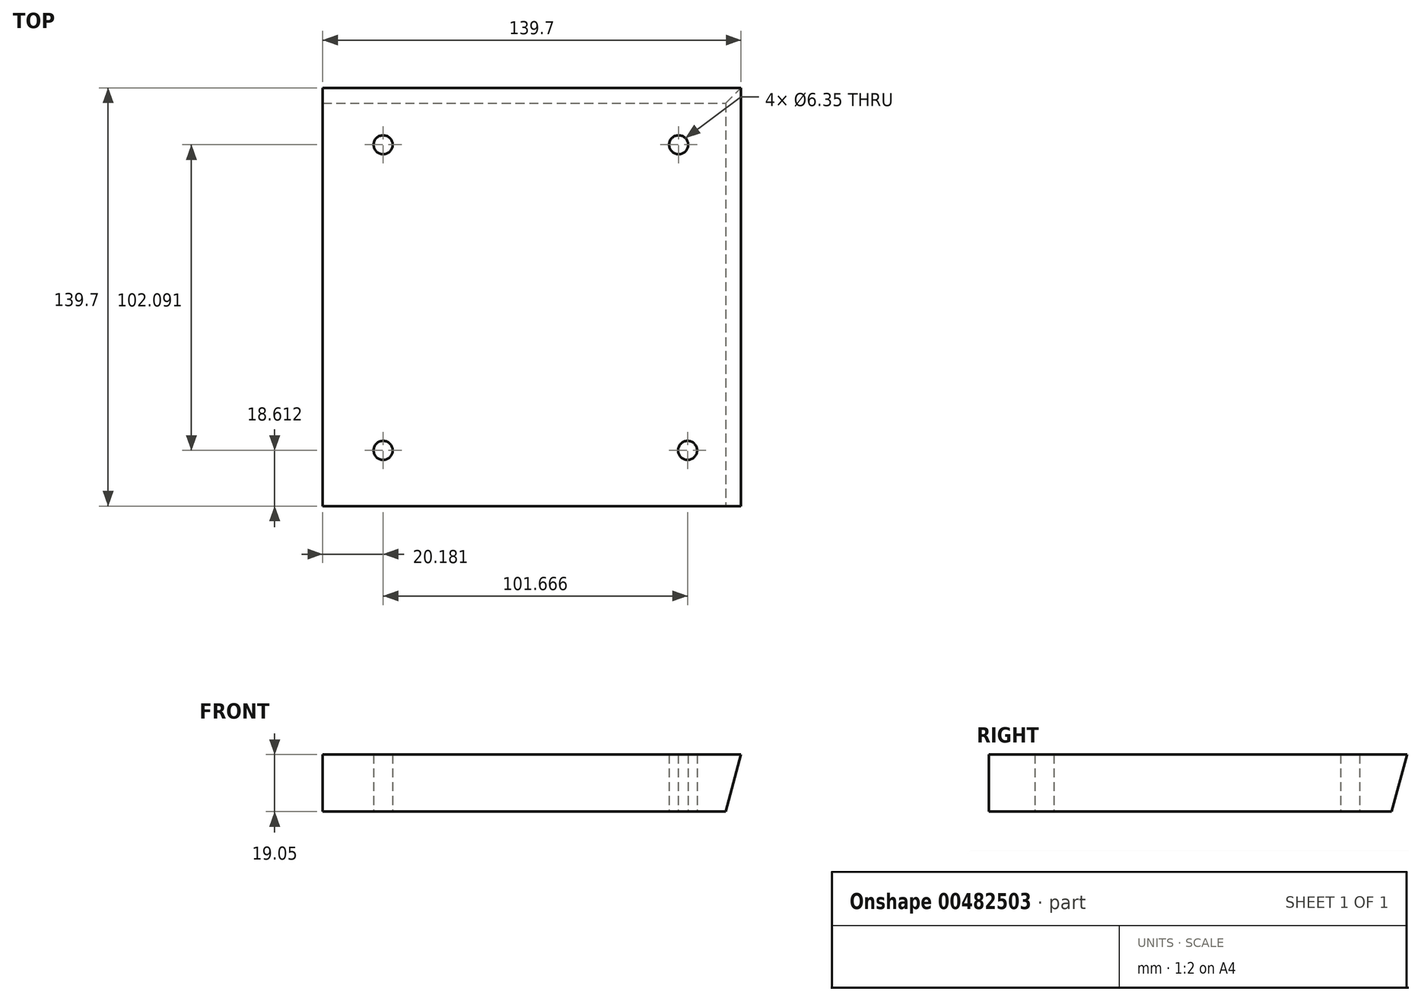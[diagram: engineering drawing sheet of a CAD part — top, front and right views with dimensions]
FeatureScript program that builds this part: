
annotation { "Feature Type Name" : "Feature", "Feature Type Description" : "" }
export const myFeature = defineFeature(function(context is Context, id is Id, definition is map)
    precondition{}
    {
        {
            var Q0;
            Q0=qCreatedBy(makeId("Top.planeOp"),FACE);
            var sketch = newSketch(context, id + "F0", { "sketchPlane" : qUnion([Q0])});
            skLineSegment(sketch, "E0.bottom", {"start": v(-73.3, 103.88) * mm, "end": v(66.4, 103.88) * mm});
            skLineSegment(sketch, "E0.top", {"start": v(-73.3, -35.82) * mm, "end": v(66.4, -35.82) * mm});
            skLineSegment(sketch, "E0.left", {"start": v(-73.3, 103.88) * mm, "end": v(-73.3, -35.82) * mm});
            skLineSegment(sketch, "E0.right", {"start": v(66.4, 103.88) * mm, "end": v(66.4, -35.82) * mm});
            skCircle(sketch, "E1", {"center": v(-53.13, -17.2) * mm, "radius": 3.18 * mm});
            skCircle(sketch, "E2", {"center": v(-53.13, 84.88) * mm, "radius": 3.18 * mm});
            skCircle(sketch, "E3", {"center": v(45.56, 84.88) * mm, "radius": 3.18 * mm});
            skCircle(sketch, "E4", {"center": v(48.54, -17.2) * mm, "radius": 3.18 * mm});
            skSolve(sketch);
        }
        {
            var Q0;
            Q0=makeQuery(id+"F0.imprint","IMPRINT",FACE,{"disambiguationData":[TD([[makeQuery(id+"F0.imprint","IMPRINT",EDGE,{"derivedFrom":sQuery(id+"F0.wireOp",EDGE,"E0.bottom")}),-1.0]])]});
            extrude(context, id + "F1", {"entities" : qUnion([Q0]), "depth" : 19.05 * mm});
        }
        {
            var Q0;
            Q0=makeQuery(id+"F1.opExtrude","CAP_EDGE",EDGE,{"disambiguationData":[OSD([sQuery(id+"F0.wireOp",EDGE,"E0.right")])],"isStart":true});
            var Q1;
            Q1=makeQuery(id+"F1.opExtrude","CAP_EDGE",EDGE,{"disambiguationData":[OSD([sQuery(id+"F0.wireOp",EDGE,"E0.bottom")])],"isStart":true});
            chamfer(context, id + "F2", {"entities" : qUnion([Q0, Q1]), "chamferType" : ChamferType.OFFSET_ANGLE, "width" : 19.05 * mm, "oppositeDirection" : true, "angle" : 15 * degree, "tangentPropagation" : true});
        }
    });
